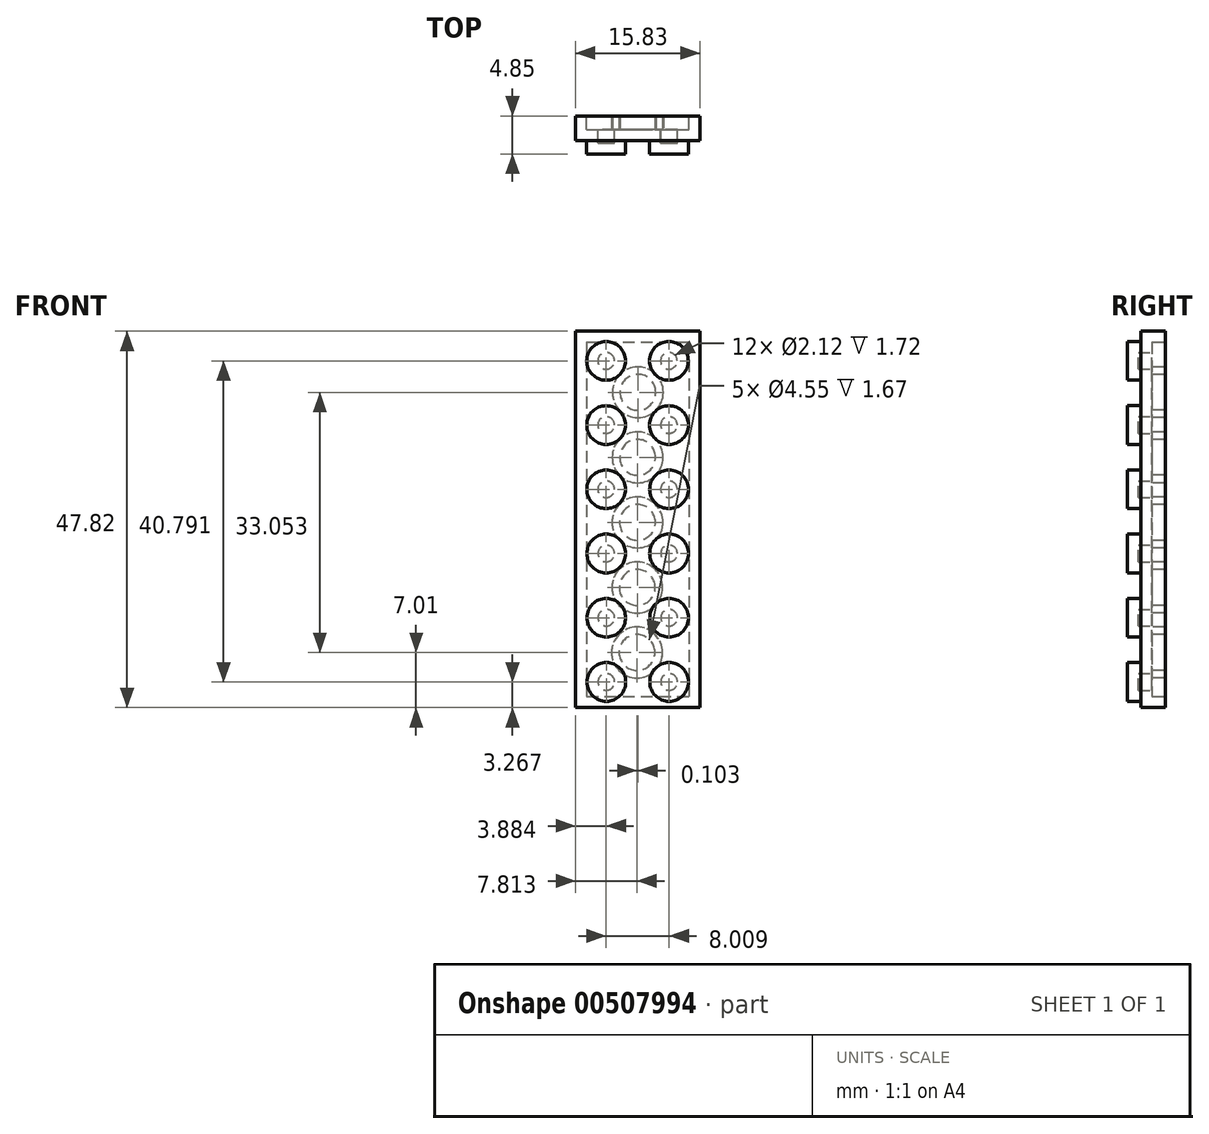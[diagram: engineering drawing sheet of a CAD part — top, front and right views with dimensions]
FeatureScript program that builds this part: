
annotation { "Feature Type Name" : "Feature", "Feature Type Description" : "" }
export const myFeature = defineFeature(function(context is Context, id is Id, definition is map)
    precondition{}
    {
        {
            var Q0;
            Q0=qCreatedBy(makeId("Front.planeOp"),FACE);
            var sketch = newSketch(context, id + "F0", { "sketchPlane" : qUnion([Q0])});
            skLineSegment(sketch, "E0", {"start": v(-21.79, 34.52) * mm, "end": v(-5.96, 34.52) * mm});
            skLineSegment(sketch, "E1", {"start": v(-21.79, -13.3) * mm, "end": v(-5.96, -13.3) * mm});
            skLineSegment(sketch, "E2", {"start": v(-21.79, 34.52) * mm, "end": v(-21.79, -13.3) * mm});
            skLineSegment(sketch, "E3", {"start": v(-5.96, 34.52) * mm, "end": v(-5.96, -13.3) * mm});
            skSolve(sketch);
        }
        {
            var Q0;
            Q0 = qSketchRegion(id + "F0", true);
            extrude(context, id + "F1", {"entities" : qUnion([Q0]), "depth" : 3.13 * mm, "offsetDistance" : 25 * mm});
        }
        {
            var Q0;
            Q0=makeQuery(id+"F1.opExtrude","CAP_FACE",FACE,{"disambiguationData":[OSD([sQuery(id+"F0.wireOp",EDGE,"E0"),sQuery(id+"F0.wireOp",EDGE,"E1"),sQuery(id+"F0.wireOp",EDGE,"E2"),sQuery(id+"F0.wireOp",EDGE,"E3")])],"isStart":false});
            var sketch = newSketch(context, id + "F2", { "sketchPlane" : qUnion([Q0])});
            skCircle(sketch, "E4", {"center": v(-17.9, 30.76) * mm, "radius": 2.46 * mm});
            skCircle(sketch, "E5", {"center": v(-9.93, 30.76) * mm, "radius": 2.46 * mm});
            skCircle(sketch, "E6.1.0.0", {"center": v(-17.9, 22.6) * mm, "radius": 2.46 * mm});
            skCircle(sketch, "E6.1.0.1", {"center": v(-9.92, 22.6) * mm, "radius": 2.46 * mm});
            skCircle(sketch, "E6.2.0.0", {"center": v(-17.9, 14.44) * mm, "radius": 2.46 * mm});
            skCircle(sketch, "E6.2.0.1", {"center": v(-9.91, 14.44) * mm, "radius": 2.46 * mm});
            skCircle(sketch, "E6.3.0.0", {"center": v(-17.89, 6.28) * mm, "radius": 2.46 * mm});
            skCircle(sketch, "E6.3.0.1", {"center": v(-9.9, 6.28) * mm, "radius": 2.46 * mm});
            skCircle(sketch, "E6.4.0.0", {"center": v(-17.88, -1.87) * mm, "radius": 2.46 * mm});
            skCircle(sketch, "E6.4.0.1", {"center": v(-9.9, -1.87) * mm, "radius": 2.46 * mm});
            skCircle(sketch, "E6.5.0.0", {"center": v(-17.88, -10.03) * mm, "radius": 2.46 * mm});
            skCircle(sketch, "E6.5.0.1", {"center": v(-9.9, -10.03) * mm, "radius": 2.46 * mm});
            skLineSegment(sketch, "E6.direction1", {"start": v(-17.9, 30.76) * mm, "end": v(-17.9, 22.6) * mm, "construction": true});
            skSolve(sketch);
        }
        {
            var Q0;
            Q0 = qSketchRegion(id + "F2", true);
            extrude(context, id + "F3", {"entities" : qUnion([Q0]), "operationType" : NewBodyOperationType.ADD, "depth" : 1.72 * mm, "offsetDistance" : 25 * mm});
        }
        {
            var Q0;
            Q0=makeQuery(id+"F1.opExtrude","CAP_FACE",FACE,{"disambiguationData":[OSD([sQuery(id+"F0.wireOp",EDGE,"E0"),sQuery(id+"F0.wireOp",EDGE,"E1"),sQuery(id+"F0.wireOp",EDGE,"E2"),sQuery(id+"F0.wireOp",EDGE,"E3")])],"isStart":true});
            shell(context, id + "F4", {"entities" : qUnion([Q0]), "thickness" : 1.4 * mm});
        }
        {
            var Q0;
            Q0=makeQuery(id+"F4.opShell","OFFSET_FACE",FACE,{"disambiguationData":[OSD([sQuery(id+"F0.wireOp",EDGE,"E0"),sQuery(id+"F0.wireOp",EDGE,"E1"),sQuery(id+"F0.wireOp",EDGE,"E2"),sQuery(id+"F0.wireOp",EDGE,"E3")])]});
            var sketch = newSketch(context, id + "F5", { "sketchPlane" : qUnion([Q0])});
            skCircle(sketch, "E7", {"center": v(13.87, 26.76) * mm, "radius": 3.23 * mm});
            skCircle(sketch, "E8", {"center": v(13.87, 26.76) * mm, "radius": 2.27 * mm});
            skCircle(sketch, "E9.1.0.0", {"center": v(13.9, 18.5) * mm, "radius": 2.27 * mm});
            skCircle(sketch, "E9.1.0.1", {"center": v(13.9, 18.5) * mm, "radius": 3.23 * mm});
            skCircle(sketch, "E9.2.0.0", {"center": v(13.93, 10.24) * mm, "radius": 2.27 * mm});
            skCircle(sketch, "E9.2.0.1", {"center": v(13.93, 10.24) * mm, "radius": 3.23 * mm});
            skCircle(sketch, "E9.3.0.0", {"center": v(13.95, 1.97) * mm, "radius": 2.27 * mm});
            skCircle(sketch, "E9.3.0.1", {"center": v(13.95, 1.97) * mm, "radius": 3.23 * mm});
            skCircle(sketch, "E9.4.0.0", {"center": v(13.98, -6.29) * mm, "radius": 2.27 * mm});
            skCircle(sketch, "E9.4.0.1", {"center": v(13.98, -6.29) * mm, "radius": 3.23 * mm});
            skLineSegment(sketch, "E9.direction1", {"start": v(13.87, 26.76) * mm, "end": v(13.9, 18.5) * mm, "construction": true});
            skSolve(sketch);
        }
        {
            var Q0;
            Q0 = qSketchRegion(id + "F5", true);
            extrude(context, id + "F6", {"entities" : qUnion([Q0]), "operationType" : NewBodyOperationType.ADD, "depth" : 1.67 * mm, "offsetDistance" : 25 * mm});
        }
    });
